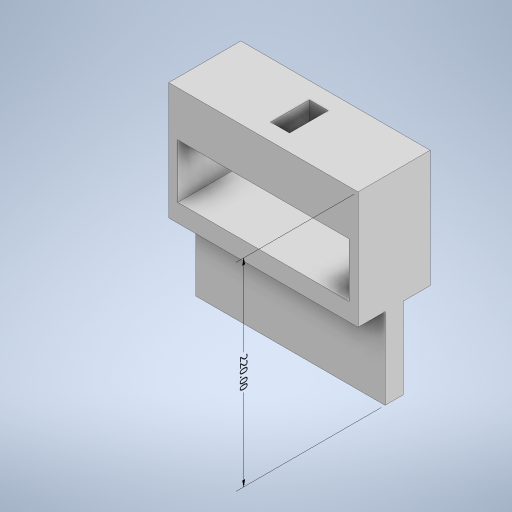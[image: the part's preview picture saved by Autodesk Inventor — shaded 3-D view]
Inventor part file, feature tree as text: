
AUTODESK INVENTOR PART (.ipt)
format: ipt  version: 2023 (Build 270158000, 158)  size: 306,688 bytes
history: native  units: mm
features: extrude x6, sketch x6, other x4, plane x2
ambient origin geometry x8: Origin, YZ Plane, XZ Plane, XY Plane, X Axis, Y Axis, Z Axis, Center Point
bodies: Body1 (feature_tree), Body2 (feature_tree)
feature tree (18):
  other  "Sólido1"
  other  "Anotaciones"
  extrude  "Extrusión1"  Depth=80.0mm
  extrude  "Extrusión2"  Depth=190.0mm
  extrude  "Extrusión3"  Depth=20.0mm
  extrude  "Extrusión4"  Depth=21.0mm
  plane  "Plano de trabajo1"
  extrude  "Extrusión6"  Depth=20.0mm
  plane  "Plano de trabajo3"
  extrude  "Extrusión7"  [1 undecoded]
  sketch  "Boceto1"  dims[d0=210.0mm d1=80.0mm]
  sketch  "Boceto2"  dims[d2=130.0mm d3=0.0mm d4=190.0mm]
  sketch  "Boceto3"  dims[d5=60.0mm d6=20.0mm]
  sketch  "Boceto4"  dims[d7=60.0mm d8=0.0mm d9=21.0mm d10=43.0mm]
  sketch  "Boceto7"  dims[d11=43.0mm d12=0.0mm d13=20.0mm]
  other  "Sólido3"
  sketch  "Boceto10"  dims[d14=90.0mm d15=0.0mm d16=-90.0mm d28=20.0mm d29=20.0mm d30=30.0mm d31=30.0mm d32=20.0mm d33=35.0mm d34=35.0mm d35=69.0mm d36=10.0mm d37=0.0mm d45=1.5mm d50=10.0mm d51=0.0mm d38=3.166395mm d39=4.283575mm d40=220.0mm]
  other  "Cota lineal 1"
note: 1 required parameter value undecoded (feature->parameter linkage not recoverable at this tier; creation-order binding heuristic only, values carry confidence <= 0.55)
